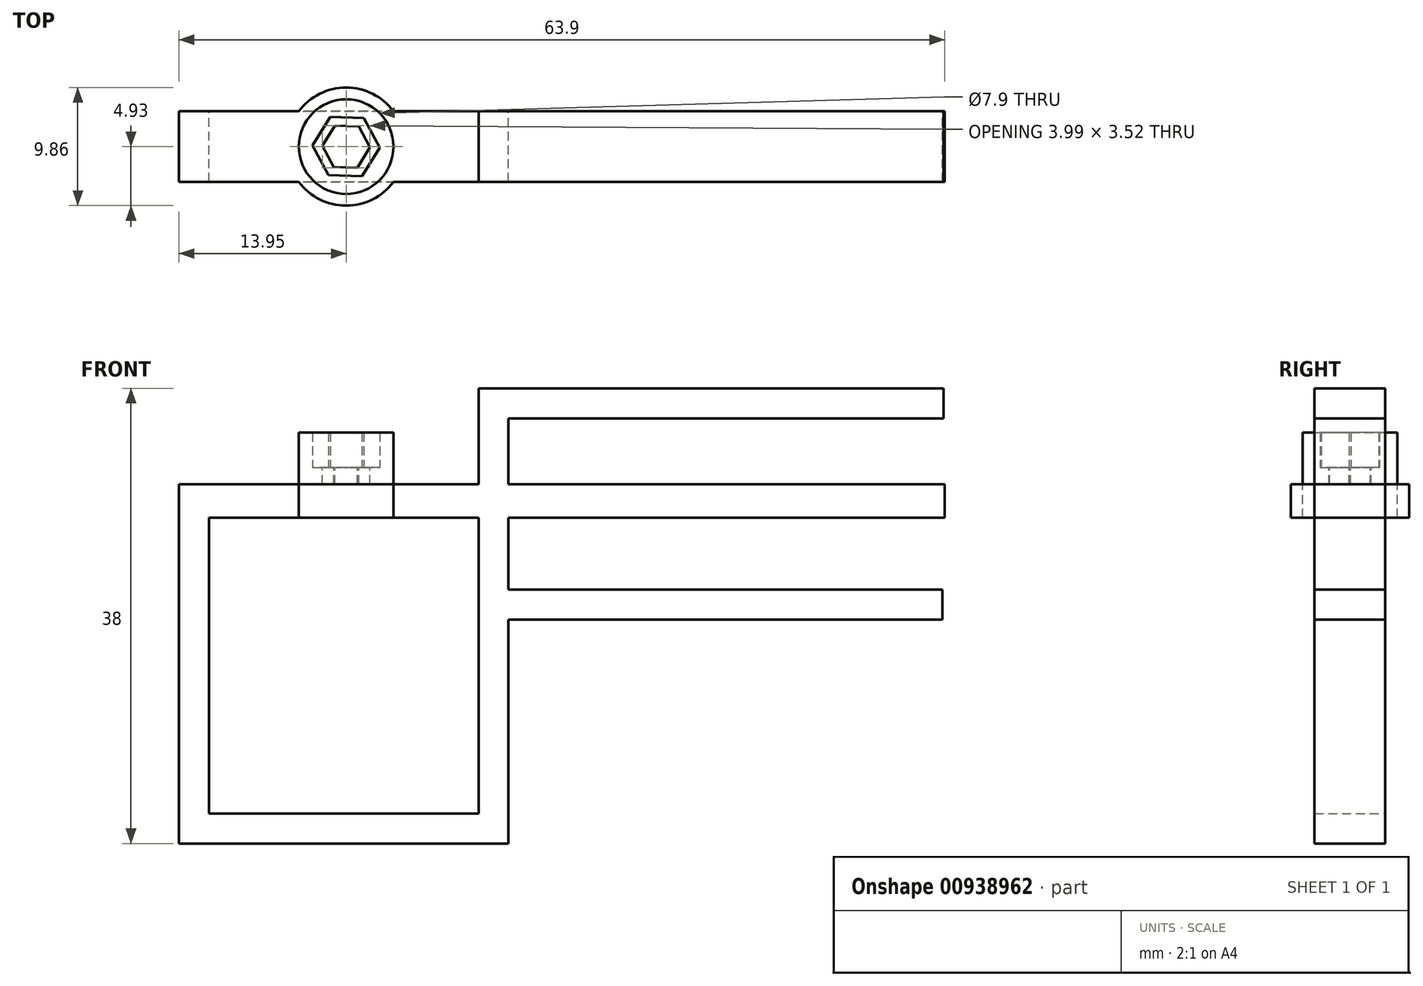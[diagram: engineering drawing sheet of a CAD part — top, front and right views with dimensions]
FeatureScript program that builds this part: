
annotation { "Feature Type Name" : "Feature", "Feature Type Description" : "" }
export const myFeature = defineFeature(function(context is Context, id is Id, definition is map)
    precondition{}
    {
        {
            var Q0;
            Q0=qCreatedBy(makeId("Top.planeOp"),FACE);
            var sketch = newSketch(context, id + "F0", { "sketchPlane" : qUnion([Q0])});
            skCircle(sketch, "E0", {"center": v(0, 0) * mm, "radius": 3.95 * mm});
            skCircle(sketch, "E1.cCircle", {"center": v(0, 0) * mm, "radius": 2.43 * mm, "construction": true});
            skLineSegment(sketch, "E1.0", {"start": v(1.48, 2.39) * mm, "end": v(2.8, -0.09) * mm});
            skLineSegment(sketch, "E1.1", {"start": v(2.8, -0.09) * mm, "end": v(1.33, -2.48) * mm});
            skLineSegment(sketch, "E1.2", {"start": v(1.33, -2.48) * mm, "end": v(-1.48, -2.39) * mm});
            skLineSegment(sketch, "E1.3", {"start": v(-1.48, -2.39) * mm, "end": v(-2.8, 0.09) * mm});
            skLineSegment(sketch, "E1.4", {"start": v(-2.8, 0.09) * mm, "end": v(-1.33, 2.48) * mm});
            skLineSegment(sketch, "E1.5", {"start": v(-1.33, 2.48) * mm, "end": v(1.48, 2.39) * mm});
            skPoint(sketch, "E1.0.midPoint", {"position": v(2.14, 1.15) * mm});
            skSolve(sketch);
        }
        {
            var Q0;
            Q0=makeQuery(id+"F0.imprint","IMPRINT",FACE,{"disambiguationData":[TD([[makeQuery(id+"F0.imprint","IMPRINT",EDGE,{"derivedFrom":sQuery(id+"F0.wireOp",EDGE,"E0")}),1.0]])]});
            extrude(context, id + "F1", {"entities" : qUnion([Q0]), "depth" : 2.92 * mm, "offsetDistance" : 25 * mm});
        }
        {
            var Q0;
            Q0=makeQuery(id+"F1.opExtrude","CAP_FACE",FACE,{"disambiguationData":[OSD([sQuery(id+"F0.wireOp",EDGE,"E0"),sQuery(id+"F0.wireOp",EDGE,"E1.0"),sQuery(id+"F0.wireOp",EDGE,"E1.1"),sQuery(id+"F0.wireOp",EDGE,"E1.2"),sQuery(id+"F0.wireOp",EDGE,"E1.3"),sQuery(id+"F0.wireOp",EDGE,"E1.4"),sQuery(id+"F0.wireOp",EDGE,"E1.5")])],"isStart":true});
            var sketch = newSketch(context, id + "F2", { "sketchPlane" : qUnion([Q0])});
            skCircle(sketch, "E2.0", {"center": v(0, 0) * mm, "radius": 3.95 * mm});
            skCircle(sketch, "E3.cCircle", {"center": v(0, 0) * mm, "radius": 1.73 * mm, "construction": true});
            skLineSegment(sketch, "E3.0", {"start": v(0.94, 1.76) * mm, "end": v(2, 0.06) * mm});
            skLineSegment(sketch, "E3.1", {"start": v(2, 0.06) * mm, "end": v(1.05, -1.7) * mm});
            skLineSegment(sketch, "E3.2", {"start": v(1.05, -1.7) * mm, "end": v(-0.94, -1.76) * mm});
            skLineSegment(sketch, "E3.3", {"start": v(-0.94, -1.76) * mm, "end": v(-2, -0.06) * mm});
            skLineSegment(sketch, "E3.4", {"start": v(-2, -0.06) * mm, "end": v(-1.05, 1.7) * mm});
            skLineSegment(sketch, "E3.5", {"start": v(-1.05, 1.7) * mm, "end": v(0.94, 1.76) * mm});
            skPoint(sketch, "E3.0.midPoint", {"position": v(1.47, 0.9) * mm});
            skLineSegment(sketch, "E4.0", {"start": v(1.33, 2.48) * mm, "end": v(-1.48, 2.39) * mm});
            skPoint(sketch, "E5", {"position": v(-0.08, 2.43) * mm});
            skPoint(sketch, "E6", {"position": v(-0.05, 1.73) * mm});
            skSolve(sketch);
        }
        {
            var Q0;
            Q0=makeQuery(id+"F2.imprint","IMPRINT",FACE,{"disambiguationData":[TD([[makeQuery(id+"F2.imprint","IMPRINT",EDGE,{"derivedFrom":sQuery(id+"F2.wireOp",EDGE,"E2.0")}),-1.0]])]});
            var Q1;
            Q1=makeQuery(id+"F2.imprint","IMPRINT",FACE,{"disambiguationData":[TD([[makeQuery(id+"F2.imprint","IMPRINT",EDGE,{"derivedFrom":sQuery(id+"F2.wireOp",EDGE,"E3.0")}),1.0]])]});
            extrude(context, id + "F3", {"entities" : qUnion([Q0, Q1]), "operationType" : NewBodyOperationType.ADD, "depth" : 3.91 * mm, "offsetDistance" : 25 * mm});
        }
        {
            var Q0;
            Q0=makeQuery(id+"F3.opExtrude","CAP_FACE",FACE,{"disambiguationData":[OSD([sQuery(id+"F2.wireOp",EDGE,"E2.0"),sQuery(id+"F2.wireOp",EDGE,"E3.0"),sQuery(id+"F2.wireOp",EDGE,"E3.1"),sQuery(id+"F2.wireOp",EDGE,"E3.2"),sQuery(id+"F2.wireOp",EDGE,"E3.3"),sQuery(id+"F2.wireOp",EDGE,"E3.4"),sQuery(id+"F2.wireOp",EDGE,"E3.5")])],"isStart":false});
            extrude(context, id + "F4", {"entities" : qUnion([Q0]), "operationType" : NewBodyOperationType.REMOVE, "oppositeDirection" : true, "depth" : 2.52 * mm, "offsetDistance" : 25 * mm});
        }
        {
            var Q0;
            Q0=makeQuery(id+"F4.boolean.opBoolean","COPY",FACE,{"derivedFrom":makeQuery(id+"F4.opExtrude","CAP_FACE",FACE,{"disambiguationData":[OSD([sQuery(id+"F2.wireOp",EDGE,"E2.0"),sQuery(id+"F2.wireOp",EDGE,"E3.0"),sQuery(id+"F2.wireOp",EDGE,"E3.1"),sQuery(id+"F2.wireOp",EDGE,"E3.2"),sQuery(id+"F2.wireOp",EDGE,"E3.3"),sQuery(id+"F2.wireOp",EDGE,"E3.4"),sQuery(id+"F2.wireOp",EDGE,"E3.5")])],"isStart":false})});
            var sketch = newSketch(context, id + "F5", { "sketchPlane" : qUnion([Q0])});
            skCircle(sketch, "E7", {"center": v(0, 0) * mm, "radius": 4.93 * mm});
            skCircle(sketch, "E8.0", {"center": v(0, 0) * mm, "radius": 3.95 * mm});
            skSolve(sketch);
        }
        {
            var Q0;
            Q0=makeQuery(id+"F5.imprint","IMPRINT",FACE,{"disambiguationData":[TD([[makeQuery(id+"F5.imprint","IMPRINT",EDGE,{"derivedFrom":sQuery(id+"F5.wireOp",EDGE,"E8.0")}),-1.0]])]});
            var Q1;
            Q1=makeQuery(id+"F5.imprint","IMPRINT",FACE,{"disambiguationData":[TD([[makeQuery(id+"F5.imprint","IMPRINT",EDGE,{"derivedFrom":sQuery(id+"F5.wireOp",EDGE,"E7")}),1.0]])]});
            extrude(context, id + "F6", {"entities" : qUnion([Q0, Q1]), "operationType" : NewBodyOperationType.ADD, "depth" : 2.8 * mm, "offsetDistance" : 25 * mm});
        }
        {
            var Q0;
            Q0=makeQuery(id+"F5.imprint","IMPRINT",FACE,{"disambiguationData":[TD([[makeQuery(id+"F5.imprint","IMPRINT",EDGE,{"derivedFrom":sQuery(id+"F5.wireOp",EDGE,"E8.0")}),-1.0]])]});
            extrude(context, id + "F7", {"entities" : qUnion([Q0]), "operationType" : NewBodyOperationType.REMOVE, "depth" : 25 * mm, "offsetDistance" : 25 * mm});
        }
        {
            var Q0;
            Q0=makeQuery(id+"F6.opExtrude","CAP_FACE",FACE,{"disambiguationData":[OSD([sQuery(id+"F2.wireOp",EDGE,"E3.0"),sQuery(id+"F2.wireOp",EDGE,"E3.1"),sQuery(id+"F2.wireOp",EDGE,"E3.2"),sQuery(id+"F2.wireOp",EDGE,"E3.3"),sQuery(id+"F2.wireOp",EDGE,"E3.4"),sQuery(id+"F2.wireOp",EDGE,"E3.5"),sQuery(id+"F5.wireOp",EDGE,"E7")])],"isStart":false});
            var sketch = newSketch(context, id + "F8", { "sketchPlane" : qUnion([Q0])});
            skPoint(sketch, "E9", {"position": v(3.95, -2.95) * mm});
            skPoint(sketch, "E10", {"position": v(3.95, 2.95) * mm});
            skLineSegment(sketch, "E11", {"start": v(3.95, 2.95) * mm, "end": v(3.95, -2.95) * mm});
            skLineSegment(sketch, "E12", {"start": v(-3.95, 2.95) * mm, "end": v(-3.95, -2.95) * mm});
            skPoint(sketch, "E13", {"position": v(-3.95, 2.95) * mm});
            skPoint(sketch, "E14", {"position": v(-3.95, -2.95) * mm});
            skPoint(sketch, "E15", {"position": v(3.95, 0) * mm});
            skPoint(sketch, "E16", {"position": v(-3.95, 0) * mm});
            skSolve(sketch);
        }
        {
            var Q0;
            Q0=makeQuery(id+"F6.opExtrude","CAP_FACE",FACE,{"disambiguationData":[OSD([sQuery(id+"F2.wireOp",EDGE,"E3.0"),sQuery(id+"F2.wireOp",EDGE,"E3.1"),sQuery(id+"F2.wireOp",EDGE,"E3.2"),sQuery(id+"F2.wireOp",EDGE,"E3.3"),sQuery(id+"F2.wireOp",EDGE,"E3.4"),sQuery(id+"F2.wireOp",EDGE,"E3.5"),sQuery(id+"F5.wireOp",EDGE,"E7")])],"isStart":true});
            var sketch = newSketch(context, id + "F9", { "sketchPlane" : qUnion([Q0])});
            skLineSegment(sketch, "E17", {"start": v(3.95, -2.95) * mm, "end": v(3.95, 2.95) * mm});
            skPoint(sketch, "E18", {"position": v(3.95, -2.95) * mm});
            skPoint(sketch, "E19", {"position": v(3.95, 2.95) * mm});
            skPoint(sketch, "E20", {"position": v(3.95, 0) * mm});
            skLineSegment(sketch, "E21.0", {"start": v(-3.95, -2.95) * mm, "end": v(-3.95, 2.95) * mm});
            skPoint(sketch, "E21.1", {"position": v(-3.95, -2.95) * mm});
            skPoint(sketch, "E21.2", {"position": v(-3.95, 0) * mm});
            skPoint(sketch, "E21.3", {"position": v(-3.95, 2.95) * mm});
            skSolve(sketch);
        }
        {
            var Q0;
            Q0=sQuery(id+"F8.wireOp",VERTEX,"E10");
            var Q1;
            Q1=sQuery(id+"F9.wireOp",VERTEX,"E20");
            var Q2;
            Q2=sQuery(id+"F8.wireOp",VERTEX,"E9");
            cPlane(context, id + "F10", {"entities" : qUnion([Q0, Q1, Q2]), "cplaneType" : CPlaneType.THREE_POINT, "offset" : 25 * mm, "width" : 150 * mm, "height" : 150 * mm});
        }
        {
            var Q0;
            Q0=sQuery(id+"F9.wireOp",VERTEX,"E21.0.start");
            var Q1;
            Q1=sQuery(id+"F8.wireOp",VERTEX,"E16");
            var Q2;
            Q2=sQuery(id+"F9.wireOp",VERTEX,"E21.3");
            cPlane(context, id + "F11", {"entities" : qUnion([Q0, Q1, Q2]), "cplaneType" : CPlaneType.THREE_POINT, "offset" : 25 * mm, "width" : 150 * mm, "height" : 150 * mm});
        }
        {
            var Q0;
            Q0=qCreatedBy(id+"F10.planeOp",FACE);
            var sketch = newSketch(context, id + "F12", { "sketchPlane" : qUnion([Q0])});
            skLineSegment(sketch, "E22.bottom", {"start": v(-2.95, -4.2) * mm, "end": v(2.95, -4.2) * mm});
            skLineSegment(sketch, "E22.top", {"start": v(-2.95, -1.4) * mm, "end": v(2.95, -1.4) * mm});
            skLineSegment(sketch, "E22.left", {"start": v(-2.95, -4.2) * mm, "end": v(-2.95, -1.4) * mm});
            skLineSegment(sketch, "E22.right", {"start": v(2.95, -4.2) * mm, "end": v(2.95, -1.4) * mm});
            skSolve(sketch);
        }
        {
            var Q0;
            Q0 = qSketchRegion(id + "F12", true);
            extrude(context, id + "F13", {"entities" : qUnion([Q0]), "operationType" : NewBodyOperationType.ADD, "depth" : 46 * mm, "offsetDistance" : 25 * mm});
        }
        {
            var Q0;
            Q0=qCreatedBy(id+"F11.planeOp",FACE);
            var sketch = newSketch(context, id + "F14", { "sketchPlane" : qUnion([Q0])});
            skLineSegment(sketch, "E23.0", {"start": v(2.95, -4.19) * mm, "end": v(-2.95, -4.19) * mm});
            skLineSegment(sketch, "E23.1", {"start": v(2.95, -4.19) * mm, "end": v(2.95, -1.39) * mm});
            skLineSegment(sketch, "E23.2", {"start": v(2.95, -1.39) * mm, "end": v(-2.95, -1.39) * mm});
            skLineSegment(sketch, "E23.3", {"start": v(-2.95, -4.19) * mm, "end": v(-2.95, -1.39) * mm});
            skPoint(sketch, "E23.4", {"position": v(0, -1.39) * mm});
            skPoint(sketch, "E23.5", {"position": v(2.95, -2.79) * mm});
            skSolve(sketch);
        }
        {
            var Q0;
            Q0 = qSketchRegion(id + "F14", true);
            extrude(context, id + "F15", {"entities" : qUnion([Q0]), "operationType" : NewBodyOperationType.ADD, "depth" : 7.5 * mm, "offsetDistance" : 25 * mm});
        }
        {
            var Q0;
            Q0=makeQuery(id+"F15.opExtrude","CAP_FACE",FACE,{"disambiguationData":[OSD([sQuery(id+"F14.wireOp",EDGE,"E23.0"),sQuery(id+"F14.wireOp",EDGE,"E23.1"),sQuery(id+"F14.wireOp",EDGE,"E23.2"),sQuery(id+"F14.wireOp",EDGE,"E23.3")])],"isStart":false});
            var sketch = newSketch(context, id + "F16", { "sketchPlane" : qUnion([Q0])});
            skLineSegment(sketch, "E24.bottom", {"start": v(2.95, -1.39) * mm, "end": v(-2.95, -1.39) * mm});
            skLineSegment(sketch, "E24.top", {"start": v(2.95, -31.39) * mm, "end": v(-2.95, -31.39) * mm});
            skLineSegment(sketch, "E24.left", {"start": v(2.95, -1.39) * mm, "end": v(2.95, -31.39) * mm});
            skLineSegment(sketch, "E24.right", {"start": v(-2.95, -1.39) * mm, "end": v(-2.95, -31.39) * mm});
            skSolve(sketch);
        }
        {
            var Q0;
            Q0 = qSketchRegion(id + "F16", true);
            extrude(context, id + "F17", {"entities" : qUnion([Q0]), "operationType" : NewBodyOperationType.ADD, "depth" : 2.5 * mm, "offsetDistance" : 25 * mm});
        }
        {
            var Q0;
            Q0=makeQuery(id+"F17.opExtrude","CAP_FACE",FACE,{"disambiguationData":[OSD([sQuery(id+"F16.wireOp",EDGE,"E24.bottom"),sQuery(id+"F16.wireOp",EDGE,"E24.top"),sQuery(id+"F16.wireOp",EDGE,"E24.left"),sQuery(id+"F16.wireOp",EDGE,"E24.right")])],"isStart":true});
            var sketch = newSketch(context, id + "F18", { "sketchPlane" : qUnion([Q0])});
            skLineSegment(sketch, "E25.bottom", {"start": v(-2.95, -31.39) * mm, "end": v(2.95, -31.39) * mm});
            skLineSegment(sketch, "E25.top", {"start": v(-2.95, -28.9) * mm, "end": v(2.95, -28.9) * mm});
            skLineSegment(sketch, "E25.left", {"start": v(-2.95, -31.39) * mm, "end": v(-2.95, -28.9) * mm});
            skLineSegment(sketch, "E25.right", {"start": v(2.95, -31.39) * mm, "end": v(2.95, -28.9) * mm});
            skSolve(sketch);
        }
        {
            var Q0;
            Q0=makeQuery(id+"F18.imprint","IMPRINT",FACE,{"disambiguationData":[TD([[makeQuery(id+"F18.imprint","IMPRINT",EDGE,{"derivedFrom":sQuery(id+"F18.wireOp",EDGE,"E25.bottom")}),1.0]])]});
            extrude(context, id + "F19", {"entities" : qUnion([Q0]), "operationType" : NewBodyOperationType.ADD, "depth" : 25 * mm, "offsetDistance" : 25 * mm});
        }
        {
            var Q0;
            Q0=makeQuery(id+"F19.opExtrude","SWEPT_FACE",FACE,{"disambiguationData":[OSD([sQuery(id+"F18.wireOp",EDGE,"E25.top")])]});
            var sketch = newSketch(context, id + "F20", { "sketchPlane" : qUnion([Q0])});
            skLineSegment(sketch, "E26.bottom", {"start": v(13.55, -2.95) * mm, "end": v(11.05, -2.95) * mm});
            skLineSegment(sketch, "E26.top", {"start": v(13.55, 2.95) * mm, "end": v(11.05, 2.95) * mm});
            skLineSegment(sketch, "E26.left", {"start": v(13.55, -2.95) * mm, "end": v(13.55, 2.95) * mm});
            skLineSegment(sketch, "E26.right", {"start": v(11.05, -2.95) * mm, "end": v(11.05, 2.95) * mm});
            skSolve(sketch);
        }
        {
            var Q0;
            Q0 = qSketchRegion(id + "F20", true);
            extrude(context, id + "F21", {"entities" : qUnion([Q0]), "operationType" : NewBodyOperationType.ADD, "depth" : 25.7 * mm, "offsetDistance" : 25 * mm});
        }
        {
            var Q0;
            Q0=makeQuery(id+"F21.boolean.opBoolean","MERGE",FACE,{"derivedFrom":[makeQuery(id+"F19.opExtrude","CAP_FACE",FACE,{"disambiguationData":[OSD([sQuery(id+"F18.wireOp",EDGE,"E25.bottom"),sQuery(id+"F18.wireOp",EDGE,"E25.top"),sQuery(id+"F18.wireOp",EDGE,"E25.left"),sQuery(id+"F18.wireOp",EDGE,"E25.right")])],"isStart":false}),makeQuery(id+"F21.opExtrude","SWEPT_FACE",FACE,{"disambiguationData":[OSD([sQuery(id+"F20.wireOp",EDGE,"E26.left")])]})]});
            var sketch = newSketch(context, id + "F22", { "sketchPlane" : qUnion([Q0])});
            skLineSegment(sketch, "E27.bottom", {"start": v(-2.95, -12.7) * mm, "end": v(2.95, -12.7) * mm});
            skLineSegment(sketch, "E27.top", {"start": v(-2.95, -10.2) * mm, "end": v(2.95, -10.2) * mm});
            skLineSegment(sketch, "E27.left", {"start": v(-2.95, -12.7) * mm, "end": v(-2.95, -10.2) * mm});
            skLineSegment(sketch, "E27.right", {"start": v(2.95, -12.7) * mm, "end": v(2.95, -10.2) * mm});
            skSolve(sketch);
        }
        {
            var Q0;
            Q0 = qSketchRegion(id + "F22", true);
            extrude(context, id + "F23", {"entities" : qUnion([Q0]), "operationType" : NewBodyOperationType.ADD, "depth" : 36.2 * mm, "offsetDistance" : 25 * mm});
        }
        {
            var Q0;
            Q0=makeQuery(id+"F17.boolean.opBoolean","MERGE",FACE,{"derivedFrom":[makeQuery(id+"F15.boolean.opBoolean","MERGE",FACE,{"derivedFrom":[makeQuery(id+"F13.boolean.opBoolean","MERGE",FACE,{"derivedFrom":[makeQuery(id+"F6.opExtrude","CAP_FACE",FACE,{"disambiguationData":[OSD([sQuery(id+"F2.wireOp",EDGE,"E3.0"),sQuery(id+"F2.wireOp",EDGE,"E3.1"),sQuery(id+"F2.wireOp",EDGE,"E3.2"),sQuery(id+"F2.wireOp",EDGE,"E3.3"),sQuery(id+"F2.wireOp",EDGE,"E3.4"),sQuery(id+"F2.wireOp",EDGE,"E3.5"),sQuery(id+"F5.wireOp",EDGE,"E7")])],"isStart":true}),makeQuery(id+"F13.opExtrude","SWEPT_FACE",FACE,{"disambiguationData":[OSD([sQuery(id+"F12.wireOp",EDGE,"E22.top")])]})]}),makeQuery(id+"F15.opExtrude","SWEPT_FACE",FACE,{"disambiguationData":[OSD([sQuery(id+"F14.wireOp",EDGE,"E23.2")])]})]}),makeQuery(id+"F17.opExtrude","SWEPT_FACE",FACE,{"disambiguationData":[OSD([sQuery(id+"F16.wireOp",EDGE,"E24.bottom")])]})]});
            var sketch = newSketch(context, id + "F24", { "sketchPlane" : qUnion([Q0])});
            skLineSegment(sketch, "E28.bottom", {"start": v(13.55, -2.95) * mm, "end": v(11.05, -2.95) * mm});
            skLineSegment(sketch, "E28.top", {"start": v(13.55, 2.95) * mm, "end": v(11.05, 2.95) * mm});
            skLineSegment(sketch, "E28.left", {"start": v(13.55, -2.95) * mm, "end": v(13.55, 2.95) * mm});
            skLineSegment(sketch, "E28.right", {"start": v(11.05, -2.95) * mm, "end": v(11.05, 2.95) * mm});
            skSolve(sketch);
        }
        {
            var Q0;
            Q0 = qSketchRegion(id + "F24", true);
            extrude(context, id + "F25", {"entities" : qUnion([Q0]), "operationType" : NewBodyOperationType.ADD, "depth" : 8 * mm, "offsetDistance" : 25 * mm});
        }
        {
            var Q0;
            Q0=makeQuery(id+"F25.opExtrude","SWEPT_FACE",FACE,{"disambiguationData":[OSD([sQuery(id+"F24.wireOp",EDGE,"E28.left")])]});
            var sketch = newSketch(context, id + "F26", { "sketchPlane" : qUnion([Q0])});
            skLineSegment(sketch, "E29.bottom", {"start": v(2.95, 6.61) * mm, "end": v(-2.95, 6.61) * mm});
            skLineSegment(sketch, "E29.top", {"start": v(2.95, 4.11) * mm, "end": v(-2.95, 4.11) * mm});
            skLineSegment(sketch, "E29.left", {"start": v(2.95, 6.61) * mm, "end": v(2.95, 4.11) * mm});
            skLineSegment(sketch, "E29.right", {"start": v(-2.95, 6.61) * mm, "end": v(-2.95, 4.1) * mm});
            skSolve(sketch);
        }
        {
            var Q0;
            Q0 = qSketchRegion(id + "F26", true);
            extrude(context, id + "F27", {"entities" : qUnion([Q0]), "operationType" : NewBodyOperationType.ADD, "depth" : 36.3 * mm, "offsetDistance" : 25 * mm});
        }
    });
